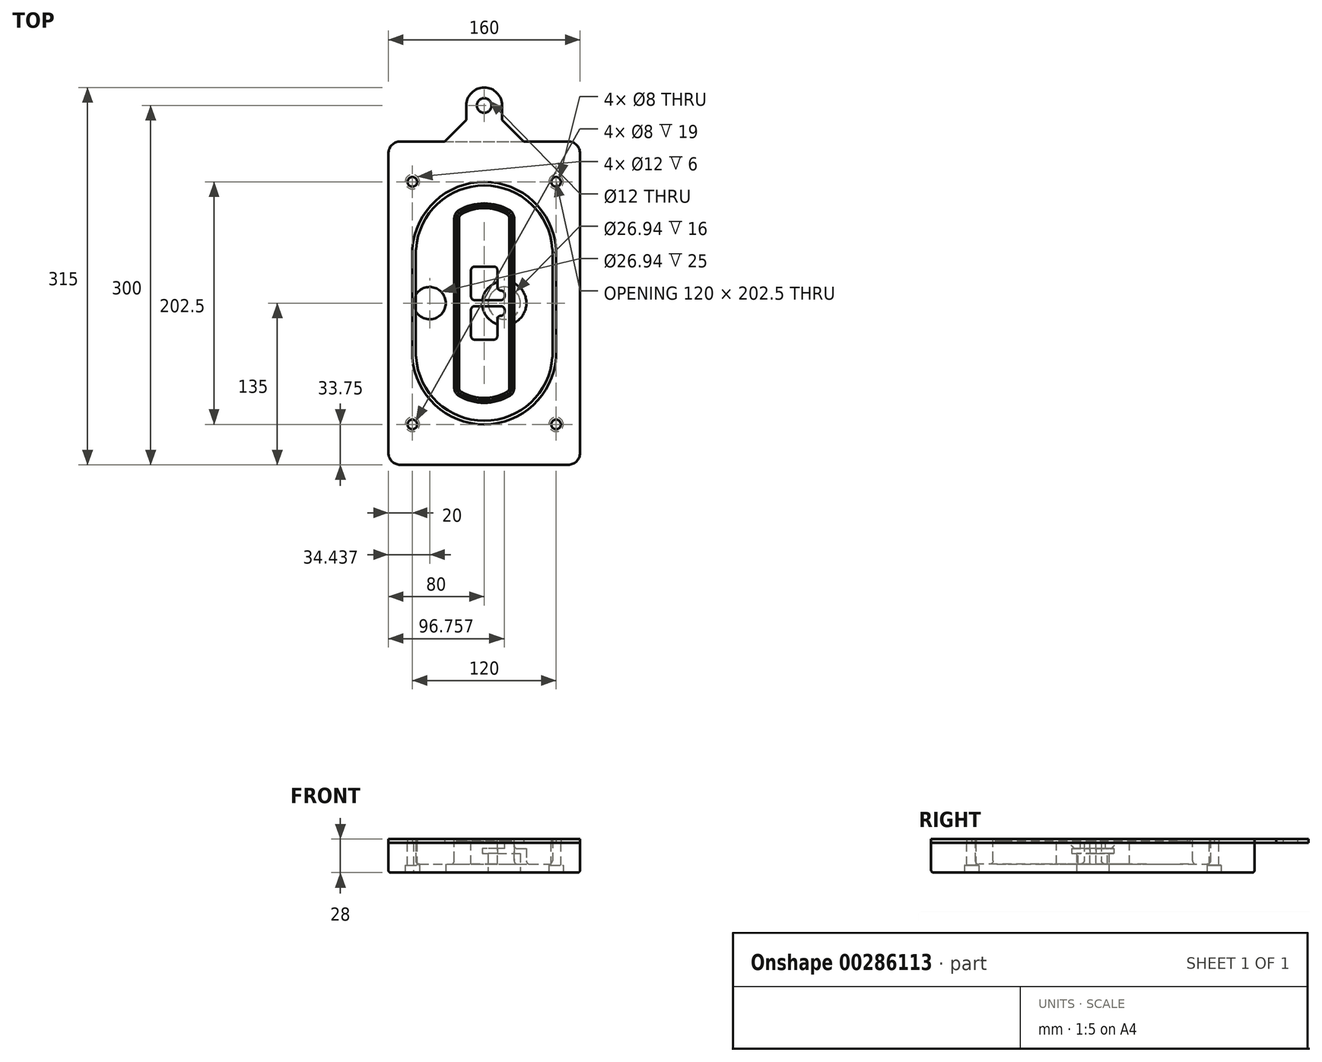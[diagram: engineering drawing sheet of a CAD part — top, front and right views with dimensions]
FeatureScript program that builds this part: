
annotation { "Feature Type Name" : "Feature", "Feature Type Description" : "" }
export const myFeature = defineFeature(function(context is Context, id is Id, definition is map)
    precondition{}
    {
        {
            var Q0;
            Q0=qCreatedBy(makeId("Top.planeOp"),FACE);
            var sketch = newSketch(context, id + "F0", { "sketchPlane" : qUnion([Q0])});
            skPoint(sketch, "E0.rect.middle", {"position": v(0, 0) * mm});
            skLineSegment(sketch, "E1.bottom", {"start": v(-70, -135) * mm, "end": v(70, -135) * mm});
            skLineSegment(sketch, "E1.top", {"start": v(-70, 135) * mm, "end": v(70, 135) * mm});
            skLineSegment(sketch, "E1.left", {"start": v(-80, -125) * mm, "end": v(-80, 125) * mm});
            skLineSegment(sketch, "E1.right", {"start": v(80, -125) * mm, "end": v(80, 125) * mm});
            skLineSegment(sketch, "E2", {"start": v(-80, 135) * mm, "end": v(80, -135) * mm, "construction": true});
            skLineSegment(sketch, "E3", {"start": v(80, 135) * mm, "end": v(-80, -135) * mm, "construction": true});
            skCircle(sketch, "E4", {"center": v(-60, 101.25) * mm, "radius": 4 * mm});
            skCircle(sketch, "E5", {"center": v(60, 101.25) * mm, "radius": 4 * mm});
            skCircle(sketch, "E6", {"center": v(60, -101.25) * mm, "radius": 4 * mm});
            skCircle(sketch, "E7", {"center": v(-60, -101.25) * mm, "radius": 4 * mm});
            skLineSegment(sketch, "E8", {"start": v(-60, 101.25) * mm, "end": v(60, 101.25) * mm, "construction": true});
            skLineSegment(sketch, "E9", {"start": v(60, 101.25) * mm, "end": v(60, -101.25) * mm, "construction": true});
            skLineSegment(sketch, "E10", {"start": v(60, -101.25) * mm, "end": v(-60, -101.25) * mm, "construction": true});
            skLineSegment(sketch, "E11", {"start": v(-60, -101.25) * mm, "end": v(-60, 101.25) * mm, "construction": true});
            skLineSegment(sketch, "E12", {"start": v(-60, 44.66) * mm, "end": v(-60, -44.66) * mm});
            skLineSegment(sketch, "E13", {"start": v(60, 44.66) * mm, "end": v(60, -44.66) * mm});
            skArc(sketch, "E14", {"start": v(59.98, 45.37) * mm, "mid": v(0, 101.25) * mm, "end": v(-59.98, 45.37) * mm});
            skArc(sketch, "E15", {"start": v(-59.98, -45.37) * mm, "mid": v(0, -101.25) * mm, "end": v(59.98, -45.37) * mm});
            skLineSegment(sketch, "E16", {"start": v(-60, 0) * mm, "end": v(60, 0) * mm, "construction": true});
            skPoint(sketch, "E17.visualSharp", {"position": v(-60, -45) * mm});
            skArc(sketch, "E17.filletArc", {"start": v(-60, -44.66) * mm, "mid": v(-60, -45.02) * mm, "end": v(-59.98, -45.37) * mm});
            skPoint(sketch, "E18.visualSharp", {"position": v(-60, 45) * mm});
            skArc(sketch, "E18.filletArc", {"start": v(-59.98, 45.37) * mm, "mid": v(-60, 45.02) * mm, "end": v(-60, 44.66) * mm});
            skPoint(sketch, "E19.visualSharp", {"position": v(60, 45) * mm});
            skArc(sketch, "E19.filletArc", {"start": v(60, 44.66) * mm, "mid": v(60, 45.02) * mm, "end": v(59.98, 45.37) * mm});
            skPoint(sketch, "E20.visualSharp", {"position": v(60, -45) * mm});
            skArc(sketch, "E20.filletArc", {"start": v(59.98, -45.37) * mm, "mid": v(60, -45.02) * mm, "end": v(60, -44.66) * mm});
            skPoint(sketch, "E21.visualSharp", {"position": v(-80, 135) * mm});
            skArc(sketch, "E21.filletArc", {"start": v(-70, 135) * mm, "mid": v(-77.07, 132.07) * mm, "end": v(-80, 125) * mm});
            skPoint(sketch, "E22.visualSharp", {"position": v(80, 135) * mm});
            skArc(sketch, "E22.filletArc", {"start": v(80, 125) * mm, "mid": v(77.07, 132.07) * mm, "end": v(70, 135) * mm});
            skPoint(sketch, "E23.visualSharp", {"position": v(80, -135) * mm});
            skArc(sketch, "E23.filletArc", {"start": v(70, -135) * mm, "mid": v(77.07, -132.07) * mm, "end": v(80, -125) * mm});
            skPoint(sketch, "E24.visualSharp", {"position": v(-80, -135) * mm});
            skArc(sketch, "E24.filletArc", {"start": v(-80, -125) * mm, "mid": v(-77.07, -132.07) * mm, "end": v(-70, -135) * mm});
            skArc(sketch, "E25.0", {"start": v(57, 44.66) * mm, "mid": v(57, 44.9) * mm, "end": v(56.98, 45.16) * mm});
            skLineSegment(sketch, "E25.1", {"start": v(57, 44.66) * mm, "end": v(57, -44.66) * mm});
            skArc(sketch, "E25.2", {"start": v(56.98, -45.16) * mm, "mid": v(57, -44.9) * mm, "end": v(57, -44.66) * mm});
            skArc(sketch, "E25.3", {"start": v(-56.98, -45.16) * mm, "mid": v(0, -98.25) * mm, "end": v(56.98, -45.16) * mm});
            skArc(sketch, "E25.4", {"start": v(-57, -44.66) * mm, "mid": v(-57, -44.9) * mm, "end": v(-56.98, -45.16) * mm});
            skArc(sketch, "E25.5", {"start": v(56.98, 45.16) * mm, "mid": v(0, 98.25) * mm, "end": v(-56.98, 45.16) * mm});
            skLineSegment(sketch, "E25.6", {"start": v(-57, 44.66) * mm, "end": v(-57, -44.66) * mm});
            skArc(sketch, "E25.7", {"start": v(-56.98, 45.16) * mm, "mid": v(-57, 44.9) * mm, "end": v(-57, 44.66) * mm});
            skArc(sketch, "E26.0", {"start": v(-63.97, 45.65) * mm, "mid": v(-64, 45.16) * mm, "end": v(-64, 44.66) * mm});
            skArc(sketch, "E26.1", {"start": v(63.97, 45.65) * mm, "mid": v(0, 105.25) * mm, "end": v(-63.97, 45.65) * mm});
            skArc(sketch, "E26.2", {"start": v(64, 44.66) * mm, "mid": v(64, 45.16) * mm, "end": v(63.97, 45.65) * mm});
            skLineSegment(sketch, "E26.3", {"start": v(64, 44.66) * mm, "end": v(64, -44.66) * mm});
            skArc(sketch, "E26.4", {"start": v(63.97, -45.65) * mm, "mid": v(64, -45.16) * mm, "end": v(64, -44.66) * mm});
            skLineSegment(sketch, "E26.5", {"start": v(-64, 44.66) * mm, "end": v(-64, -44.66) * mm});
            skArc(sketch, "E26.6", {"start": v(-63.97, -45.65) * mm, "mid": v(0, -105.25) * mm, "end": v(63.97, -45.65) * mm});
            skArc(sketch, "E26.7", {"start": v(-64, -44.66) * mm, "mid": v(-64, -45.16) * mm, "end": v(-63.97, -45.65) * mm});
            skSolve(sketch);
        }
        {
            var Q0;
            Q0=makeQuery(id+"F0.imprint","IMPRINT",FACE,{"disambiguationData":[TD([[makeQuery(id+"F0.imprint","IMPRINT",EDGE,{"derivedFrom":sQuery(id+"F0.wireOp",EDGE,"E1.bottom")}),1.0]])]});
            var Q1;
            Q1=makeQuery(id+"F0.imprint","IMPRINT",FACE,{"disambiguationData":[TD([[makeQuery(id+"F0.imprint","IMPRINT",EDGE,{"derivedFrom":sQuery(id+"F0.wireOp",EDGE,"E12")}),1.0]])]});
            var Q2;
            Q2=makeQuery(id+"F0.imprint","IMPRINT",FACE,{"disambiguationData":[TD([[makeQuery(id+"F0.imprint","IMPRINT",EDGE,{"derivedFrom":sQuery(id+"F0.wireOp",EDGE,"E25.0")}),1.0]])]});
            var Q3;
            Q3=makeQuery(id+"F0.imprint","IMPRINT",FACE,{"disambiguationData":[TD([[makeQuery(id+"F0.imprint","IMPRINT",EDGE,{"derivedFrom":sQuery(id+"F0.wireOp",EDGE,"E12")}),-1.0]])]});
            extrude(context, id + "F1", {"entities" : qUnion([Q0, Q1, Q2, Q3]), "oppositeDirection" : true, "depth" : 25 * mm});
        }
        {
            var Q0;
            Q0=makeQuery(id+"F0.imprint","IMPRINT",FACE,{"disambiguationData":[TD([[makeQuery(id+"F0.imprint","IMPRINT",EDGE,{"derivedFrom":sQuery(id+"F0.wireOp",EDGE,"E12")}),1.0]])]});
            extrude(context, id + "F2", {"entities" : qUnion([Q0]), "operationType" : NewBodyOperationType.ADD, "depth" : 3 * mm});
        }
        {
            var Q0;
            Q0=makeQuery(id+"F0.imprint","IMPRINT",FACE,{"disambiguationData":[TD([[makeQuery(id+"F0.imprint","IMPRINT",EDGE,{"derivedFrom":sQuery(id+"F0.wireOp",EDGE,"E25.0")}),1.0]])]});
            extrude(context, id + "F3", {"entities" : qUnion([Q0]), "operationType" : NewBodyOperationType.REMOVE, "oppositeDirection" : true, "depth" : 18 * mm});
        }
        {
            var Q0;
            Q0=makeQuery(id+"F2.opExtrude","CAP_FACE",FACE,{"disambiguationData":[OSD([sQuery(id+"F0.wireOp",EDGE,"E12"),sQuery(id+"F0.wireOp",EDGE,"E13"),sQuery(id+"F0.wireOp",EDGE,"E14"),sQuery(id+"F0.wireOp",EDGE,"E15"),sQuery(id+"F0.wireOp",EDGE,"E17.filletArc"),sQuery(id+"F0.wireOp",EDGE,"E18.filletArc"),sQuery(id+"F0.wireOp",EDGE,"E19.filletArc"),sQuery(id+"F0.wireOp",EDGE,"E20.filletArc"),sQuery(id+"F0.wireOp",EDGE,"E25.0"),sQuery(id+"F0.wireOp",EDGE,"E25.1"),sQuery(id+"F0.wireOp",EDGE,"E25.2"),sQuery(id+"F0.wireOp",EDGE,"E25.3"),sQuery(id+"F0.wireOp",EDGE,"E25.4"),sQuery(id+"F0.wireOp",EDGE,"E25.5"),sQuery(id+"F0.wireOp",EDGE,"E25.6"),sQuery(id+"F0.wireOp",EDGE,"E25.7")])],"isStart":false});
            var sketch = newSketch(context, id + "F4", { "sketchPlane" : qUnion([Q0])});
            skArc(sketch, "E27.0", {"start": v(-20.99, -77.65) * mm, "mid": v(0, -83.25) * mm, "end": v(20.99, -77.65) * mm});
            skArc(sketch, "E28.0", {"start": v(20.99, 77.65) * mm, "mid": v(0, 83.25) * mm, "end": v(-20.99, 77.65) * mm});
            skLineSegment(sketch, "E29", {"start": v(-25, 70.71) * mm, "end": v(-25, -70.71) * mm});
            skLineSegment(sketch, "E30", {"start": v(25, 70.71) * mm, "end": v(25, -70.71) * mm});
            skLineSegment(sketch, "E31", {"start": v(-25, 75.03) * mm, "end": v(25, 75.03) * mm, "construction": true});
            skLineSegment(sketch, "E32", {"start": v(-25, -75.03) * mm, "end": v(25, -75.03) * mm, "construction": true});
            skPoint(sketch, "E33.visualSharp", {"position": v(-25, 75.03) * mm});
            skArc(sketch, "E33.filletArc", {"start": v(-20.99, 77.65) * mm, "mid": v(-23.92, 74.72) * mm, "end": v(-25, 70.71) * mm});
            skPoint(sketch, "E34.visualSharp", {"position": v(25, 75.03) * mm});
            skArc(sketch, "E34.filletArc", {"start": v(25, 70.71) * mm, "mid": v(23.92, 74.72) * mm, "end": v(20.99, 77.65) * mm});
            skPoint(sketch, "E35.visualSharp", {"position": v(25, -75.03) * mm});
            skArc(sketch, "E35.filletArc", {"start": v(20.99, -77.65) * mm, "mid": v(23.92, -74.72) * mm, "end": v(25, -70.71) * mm});
            skPoint(sketch, "E36.visualSharp", {"position": v(-25, -75.03) * mm});
            skArc(sketch, "E36.filletArc", {"start": v(-25, -70.71) * mm, "mid": v(-23.92, -74.72) * mm, "end": v(-20.99, -77.65) * mm});
            skArc(sketch, "E37.0", {"start": v(56.98, 45.16) * mm, "mid": v(0, 98.25) * mm, "end": v(-56.98, 45.16) * mm});
            skArc(sketch, "E37.1", {"start": v(-56.98, 45.16) * mm, "mid": v(-57, 44.9) * mm, "end": v(-57, 44.66) * mm});
            skLineSegment(sketch, "E37.2", {"start": v(-57, 44.66) * mm, "end": v(-57, -44.66) * mm});
            skArc(sketch, "E37.3", {"start": v(-57, -44.66) * mm, "mid": v(-57, -44.9) * mm, "end": v(-56.98, -45.16) * mm});
            skArc(sketch, "E37.4", {"start": v(-56.98, -45.16) * mm, "mid": v(0, -98.25) * mm, "end": v(56.98, -45.16) * mm});
            skArc(sketch, "E37.5", {"start": v(56.98, -45.16) * mm, "mid": v(57, -44.9) * mm, "end": v(57, -44.66) * mm});
            skLineSegment(sketch, "E37.6", {"start": v(57, 44.66) * mm, "end": v(57, -44.66) * mm});
            skArc(sketch, "E37.7", {"start": v(57, 44.66) * mm, "mid": v(57, 44.9) * mm, "end": v(56.98, 45.16) * mm});
            skLineSegment(sketch, "E38.0", {"start": v(23, 70.71) * mm, "end": v(23, -70.71) * mm});
            skArc(sketch, "E38.1", {"start": v(19.99, -75.92) * mm, "mid": v(22.2, -73.72) * mm, "end": v(23, -70.71) * mm});
            skArc(sketch, "E38.2", {"start": v(-19.99, -75.92) * mm, "mid": v(0, -81.25) * mm, "end": v(19.99, -75.92) * mm});
            skArc(sketch, "E38.3", {"start": v(-23, -70.71) * mm, "mid": v(-22.2, -73.72) * mm, "end": v(-19.99, -75.92) * mm});
            skLineSegment(sketch, "E38.4", {"start": v(-23, 70.71) * mm, "end": v(-23, -70.71) * mm});
            skArc(sketch, "E38.5", {"start": v(23, 70.71) * mm, "mid": v(22.2, 73.72) * mm, "end": v(19.99, 75.92) * mm});
            skArc(sketch, "E38.6", {"start": v(-19.99, 75.92) * mm, "mid": v(-22.2, 73.72) * mm, "end": v(-23, 70.71) * mm});
            skArc(sketch, "E38.7", {"start": v(19.99, 75.92) * mm, "mid": v(0, 81.25) * mm, "end": v(-19.99, 75.92) * mm});
            skArc(sketch, "E39.0", {"start": v(21, 70.71) * mm, "mid": v(20.46, 72.72) * mm, "end": v(19, 74.18) * mm});
            skLineSegment(sketch, "E39.1", {"start": v(21, 70.71) * mm, "end": v(21, -70.71) * mm});
            skArc(sketch, "E39.2", {"start": v(19, -74.18) * mm, "mid": v(20.46, -72.72) * mm, "end": v(21, -70.71) * mm});
            skArc(sketch, "E39.3", {"start": v(-19, -74.18) * mm, "mid": v(0, -79.25) * mm, "end": v(19, -74.18) * mm});
            skArc(sketch, "E39.4", {"start": v(-21, -70.71) * mm, "mid": v(-20.46, -72.72) * mm, "end": v(-19, -74.18) * mm});
            skArc(sketch, "E39.5", {"start": v(19, 74.18) * mm, "mid": v(0, 79.25) * mm, "end": v(-19, 74.18) * mm});
            skLineSegment(sketch, "E39.6", {"start": v(-21, 70.71) * mm, "end": v(-21, -70.71) * mm});
            skArc(sketch, "E39.7", {"start": v(-19, 74.18) * mm, "mid": v(-20.46, 72.72) * mm, "end": v(-21, 70.71) * mm});
            skLineSegment(sketch, "E40", {"start": v(-25, 0) * mm, "end": v(25, 0) * mm, "construction": true});
            skLineSegment(sketch, "E41", {"start": v(-11, 5.5) * mm, "end": v(-11, 27.5) * mm});
            skLineSegment(sketch, "E42", {"start": v(-8, 30.5) * mm, "end": v(8, 30.5) * mm});
            skLineSegment(sketch, "E43", {"start": v(11, 27.5) * mm, "end": v(11, 13.5) * mm});
            skLineSegment(sketch, "E44", {"start": v(14, 10.5) * mm, "end": v(14, 10.5) * mm});
            skLineSegment(sketch, "E45", {"start": v(17, 7.5) * mm, "end": v(17, 5.5) * mm});
            skLineSegment(sketch, "E46", {"start": v(14, 2.5) * mm, "end": v(-8, 2.5) * mm});
            skPoint(sketch, "E47.visualSharp", {"position": v(-11, 30.5) * mm});
            skArc(sketch, "E47.filletArc", {"start": v(-8, 30.5) * mm, "mid": v(-10.12, 29.62) * mm, "end": v(-11, 27.5) * mm});
            skPoint(sketch, "E48.visualSharp", {"position": v(11, 30.5) * mm});
            skArc(sketch, "E48.filletArc", {"start": v(11, 27.5) * mm, "mid": v(10.12, 29.62) * mm, "end": v(8, 30.5) * mm});
            skPoint(sketch, "E49.visualSharp", {"position": v(11, 10.5) * mm});
            skArc(sketch, "E49.filletArc", {"start": v(11, 13.5) * mm, "mid": v(11.88, 11.38) * mm, "end": v(14, 10.5) * mm});
            skPoint(sketch, "E50.visualSharp", {"position": v(17, 10.5) * mm});
            skArc(sketch, "E50.filletArc", {"start": v(17, 7.5) * mm, "mid": v(16.12, 9.62) * mm, "end": v(14, 10.5) * mm});
            skPoint(sketch, "E51.visualSharp", {"position": v(17, 2.5) * mm});
            skArc(sketch, "E51.filletArc", {"start": v(14, 2.5) * mm, "mid": v(16.12, 3.38) * mm, "end": v(17, 5.5) * mm});
            skPoint(sketch, "E52.visualSharp", {"position": v(-11, 2.5) * mm});
            skArc(sketch, "E52.filletArc", {"start": v(-11, 5.5) * mm, "mid": v(-10.12, 3.38) * mm, "end": v(-8, 2.5) * mm});
            skLineSegment(sketch, "E53.0.MirrorCS", {"start": v(14, -2.5) * mm, "end": v(-8, -2.5) * mm});
            skArc(sketch, "E54.0.MirrorCS", {"start": v(-11, -5.5) * mm, "mid": v(-10.12, -3.38) * mm, "end": v(-8, -2.5) * mm});
            skLineSegment(sketch, "E55.0.MirrorCS", {"start": v(-11, -5.5) * mm, "end": v(-11, -27.5) * mm});
            skArc(sketch, "E56.0.MirrorCS", {"start": v(-8, -30.5) * mm, "mid": v(-10.12, -29.62) * mm, "end": v(-11, -27.5) * mm});
            skLineSegment(sketch, "E57.0.MirrorCS", {"start": v(-8, -30.5) * mm, "end": v(8, -30.5) * mm});
            skArc(sketch, "E58.0.MirrorCS", {"start": v(11, -27.5) * mm, "mid": v(10.12, -29.62) * mm, "end": v(8, -30.5) * mm});
            skLineSegment(sketch, "E59.0.MirrorCS", {"start": v(11, -27.5) * mm, "end": v(11, -13.5) * mm});
            skArc(sketch, "E60.0.MirrorCS", {"start": v(11, -13.5) * mm, "mid": v(11.88, -11.38) * mm, "end": v(14, -10.5) * mm});
            skArc(sketch, "E61.0.MirrorCS", {"start": v(17, -7.5) * mm, "mid": v(16.12, -9.62) * mm, "end": v(14, -10.5) * mm});
            skLineSegment(sketch, "E62.0.MirrorCS", {"start": v(17, -7.5) * mm, "end": v(17, -5.5) * mm});
            skArc(sketch, "E63.0.MirrorCS", {"start": v(14, -2.5) * mm, "mid": v(16.12, -3.38) * mm, "end": v(17, -5.5) * mm});
            skSolve(sketch);
        }
        {
            var Q0;
            Q0=makeQuery(id+"F4.imprint","IMPRINT",FACE,{"disambiguationData":[TD([[makeQuery(id+"F4.imprint","IMPRINT",EDGE,{"derivedFrom":sQuery(id+"F4.wireOp",EDGE,"E27.0")}),1.0]])]});
            var Q1;
            Q1=makeQuery(id+"F4.imprint","IMPRINT",FACE,{"disambiguationData":[TD([[makeQuery(id+"F4.imprint","IMPRINT",EDGE,{"derivedFrom":sQuery(id+"F4.wireOp",EDGE,"E38.0")}),-1.0]])]});
            var Q2;
            Q2=makeQuery(id+"F4.imprint","IMPRINT",FACE,{"disambiguationData":[TD([[makeQuery(id+"F4.imprint","IMPRINT",EDGE,{"derivedFrom":sQuery(id+"F4.wireOp",EDGE,"E39.0")}),1.0]])]});
            extrude(context, id + "F5", {"entities" : qUnion([Q0, Q1, Q2]), "operationType" : NewBodyOperationType.ADD, "endBound" : BoundingType.UP_TO_NEXT, "oppositeDirection" : true, "depth" : 25 * mm});
        }
        {
            var Q0;
            Q0=makeQuery(id+"F4.imprint","IMPRINT",FACE,{"disambiguationData":[TD([[makeQuery(id+"F4.imprint","IMPRINT",EDGE,{"derivedFrom":sQuery(id+"F4.wireOp",EDGE,"E38.0")}),-1.0]])]});
            extrude(context, id + "F6", {"entities" : qUnion([Q0]), "operationType" : NewBodyOperationType.REMOVE, "oppositeDirection" : true, "depth" : 2 * mm});
        }
        {
            var Q0;
            Q0=makeQuery(id+"F1.opExtrude","CAP_FACE",FACE,{"disambiguationData":[OSD([sQuery(id+"F0.wireOp",EDGE,"E1.bottom"),sQuery(id+"F0.wireOp",EDGE,"E1.top"),sQuery(id+"F0.wireOp",EDGE,"E1.left"),sQuery(id+"F0.wireOp",EDGE,"E1.right"),sQuery(id+"F0.wireOp",EDGE,"E4"),sQuery(id+"F0.wireOp",EDGE,"E5"),sQuery(id+"F0.wireOp",EDGE,"E6"),sQuery(id+"F0.wireOp",EDGE,"E7"),sQuery(id+"F0.wireOp",EDGE,"E21.filletArc"),sQuery(id+"F0.wireOp",EDGE,"E22.filletArc"),sQuery(id+"F0.wireOp",EDGE,"E23.filletArc"),sQuery(id+"F0.wireOp",EDGE,"E24.filletArc")])],"isStart":false});
            var sketch = newSketch(context, id + "F7", { "sketchPlane" : qUnion([Q0])});
            skCircle(sketch, "E64", {"center": v(16.76, 0) * mm, "radius": 13.47 * mm});
            skCircle(sketch, "E65", {"center": v(-45.56, 0) * mm, "radius": 13.47 * mm});
            skLineSegment(sketch, "E66", {"start": v(80, 0) * mm, "end": v(-80, 0) * mm});
            skCircle(sketch, "E67", {"center": v(16.76, 0) * mm, "radius": 18.47 * mm});
            skCircle(sketch, "E68", {"center": v(60, -101.25) * mm, "radius": 6 * mm});
            skCircle(sketch, "E69", {"center": v(-60, -101.25) * mm, "radius": 6 * mm});
            skCircle(sketch, "E70", {"center": v(-60, 101.25) * mm, "radius": 6 * mm});
            skCircle(sketch, "E71", {"center": v(60, 101.25) * mm, "radius": 6 * mm});
            skSolve(sketch);
        }
        {
            var Q0;
            {var subQ1=sQuery(id+"F7.wireOp",EDGE,"E66");var subQ4=sQuery(id+"F7.wireOp",EDGE,"E64");var subQ6=makeQuery(id+"F7.imprint","INTERSECT",VERTEX,{"disambiguationData":[OD(0.0)],"derivedFrom":[subQ4,subQ1]});Q0=makeQuery(id+"F7.imprint","IMPRINT",FACE,{"disambiguationData":[TD([[makeQuery(id+"F7.imprint","IMPRINT",EDGE,{"disambiguationData":[TD([[subQ6,-1.0]])],"derivedFrom":subQ4}),-1.0]])]});}
            var Q1;
            {var subQ0=sQuery(id+"F7.wireOp",EDGE,"E66");var subQ1=sQuery(id+"F7.wireOp",EDGE,"E64");var subQ3=makeQuery(id+"F7.imprint","INTERSECT",VERTEX,{"disambiguationData":[OD(0.0)],"derivedFrom":[subQ1,subQ0]});Q1=makeQuery(id+"F7.imprint","IMPRINT",FACE,{"disambiguationData":[TD([[makeQuery(id+"F7.imprint","IMPRINT",EDGE,{"disambiguationData":[TD([[subQ3,-1.0]])],"derivedFrom":subQ1}),1.0]])]});}
            var Q2;
            {var subQ0=sQuery(id+"F7.wireOp",EDGE,"E66");var subQ1=sQuery(id+"F7.wireOp",EDGE,"E64");var subQ3=makeQuery(id+"F7.imprint","INTERSECT",VERTEX,{"disambiguationData":[OD(0.0)],"derivedFrom":[subQ1,subQ0]});Q2=makeQuery(id+"F7.imprint","IMPRINT",FACE,{"disambiguationData":[TD([[makeQuery(id+"F7.imprint","IMPRINT",EDGE,{"disambiguationData":[TD([[subQ3,1.0]])],"derivedFrom":subQ1}),1.0]])]});}
            var Q3;
            {var subQ1=sQuery(id+"F7.wireOp",EDGE,"E66");var subQ4=sQuery(id+"F7.wireOp",EDGE,"E64");var subQ6=makeQuery(id+"F7.imprint","INTERSECT",VERTEX,{"disambiguationData":[OD(0.0)],"derivedFrom":[subQ4,subQ1]});Q3=makeQuery(id+"F7.imprint","IMPRINT",FACE,{"disambiguationData":[TD([[makeQuery(id+"F7.imprint","IMPRINT",EDGE,{"disambiguationData":[TD([[subQ6,1.0]])],"derivedFrom":subQ4}),-1.0]])]});}
            extrude(context, id + "F8", {"entities" : qUnion([Q0, Q1, Q2, Q3]), "operationType" : NewBodyOperationType.ADD, "oppositeDirection" : true, "depth" : 20 * mm});
        }
        {
            var Q0;
            {var subQ0=sQuery(id+"F7.wireOp",EDGE,"E66");var subQ1=sQuery(id+"F7.wireOp",EDGE,"E64");var subQ3=makeQuery(id+"F7.imprint","INTERSECT",VERTEX,{"disambiguationData":[OD(0.0)],"derivedFrom":[subQ1,subQ0]});Q0=makeQuery(id+"F7.imprint","IMPRINT",FACE,{"disambiguationData":[TD([[makeQuery(id+"F7.imprint","IMPRINT",EDGE,{"disambiguationData":[TD([[subQ3,-1.0]])],"derivedFrom":subQ1}),1.0]])]});}
            var Q1;
            {var subQ0=sQuery(id+"F7.wireOp",EDGE,"E66");var subQ1=sQuery(id+"F7.wireOp",EDGE,"E64");var subQ3=makeQuery(id+"F7.imprint","INTERSECT",VERTEX,{"disambiguationData":[OD(0.0)],"derivedFrom":[subQ1,subQ0]});Q1=makeQuery(id+"F7.imprint","IMPRINT",FACE,{"disambiguationData":[TD([[makeQuery(id+"F7.imprint","IMPRINT",EDGE,{"disambiguationData":[TD([[subQ3,1.0]])],"derivedFrom":subQ1}),1.0]])]});}
            extrude(context, id + "F9", {"entities" : qUnion([Q0, Q1]), "operationType" : NewBodyOperationType.REMOVE, "oppositeDirection" : true, "depth" : 16 * mm});
        }
        {
            var Q0;
            {var subQ0=sQuery(id+"F7.wireOp",EDGE,"E66");var subQ1=sQuery(id+"F7.wireOp",EDGE,"E65");var subQ3=makeQuery(id+"F7.imprint","INTERSECT",VERTEX,{"disambiguationData":[OD(0.0)],"derivedFrom":[subQ1,subQ0]});Q0=makeQuery(id+"F7.imprint","IMPRINT",FACE,{"disambiguationData":[TD([[makeQuery(id+"F7.imprint","IMPRINT",EDGE,{"disambiguationData":[TD([[subQ3,-1.0]])],"derivedFrom":subQ1}),1.0]])]});}
            var Q1;
            {var subQ0=sQuery(id+"F7.wireOp",EDGE,"E66");var subQ1=sQuery(id+"F7.wireOp",EDGE,"E65");var subQ3=makeQuery(id+"F7.imprint","INTERSECT",VERTEX,{"disambiguationData":[OD(0.0)],"derivedFrom":[subQ1,subQ0]});Q1=makeQuery(id+"F7.imprint","IMPRINT",FACE,{"disambiguationData":[TD([[makeQuery(id+"F7.imprint","IMPRINT",EDGE,{"disambiguationData":[TD([[subQ3,1.0]])],"derivedFrom":subQ1}),1.0]])]});}
            extrude(context, id + "F10", {"entities" : qUnion([Q0, Q1]), "operationType" : NewBodyOperationType.REMOVE, "oppositeDirection" : true, "depth" : 25 * mm});
        }
        {
            var Q0;
            Q0=makeQuery(id+"F7.imprint","IMPRINT",FACE,{"disambiguationData":[TD([[makeQuery(id+"F7.imprint","IMPRINT",EDGE,{"derivedFrom":sQuery(id+"F7.wireOp",EDGE,"E68")}),1.0]])]});
            var Q1;
            Q1=makeQuery(id+"F7.imprint","IMPRINT",FACE,{"disambiguationData":[TD([[makeQuery(id+"F7.imprint","IMPRINT",EDGE,{"derivedFrom":makeQuery(id+"F1.opExtrude","CAP_EDGE",EDGE,{"disambiguationData":[OSD([sQuery(id+"F0.wireOp",EDGE,"E5")])],"isStart":false})}),-1.0]])]});
            var Q2;
            Q2=makeQuery(id+"F7.imprint","IMPRINT",FACE,{"disambiguationData":[TD([[makeQuery(id+"F7.imprint","IMPRINT",EDGE,{"derivedFrom":sQuery(id+"F7.wireOp",EDGE,"E69")}),1.0]])]});
            var Q3;
            Q3=makeQuery(id+"F7.imprint","IMPRINT",FACE,{"disambiguationData":[TD([[makeQuery(id+"F7.imprint","IMPRINT",EDGE,{"derivedFrom":makeQuery(id+"F1.opExtrude","CAP_EDGE",EDGE,{"disambiguationData":[OSD([sQuery(id+"F0.wireOp",EDGE,"E4")])],"isStart":false})}),-1.0]])]});
            var Q4;
            Q4=makeQuery(id+"F7.imprint","IMPRINT",FACE,{"disambiguationData":[TD([[makeQuery(id+"F7.imprint","IMPRINT",EDGE,{"derivedFrom":sQuery(id+"F7.wireOp",EDGE,"E70")}),1.0]])]});
            var Q5;
            Q5=makeQuery(id+"F7.imprint","IMPRINT",FACE,{"disambiguationData":[TD([[makeQuery(id+"F7.imprint","IMPRINT",EDGE,{"derivedFrom":makeQuery(id+"F1.opExtrude","CAP_EDGE",EDGE,{"disambiguationData":[OSD([sQuery(id+"F0.wireOp",EDGE,"E7")])],"isStart":false})}),-1.0]])]});
            var Q6;
            Q6=makeQuery(id+"F7.imprint","IMPRINT",FACE,{"disambiguationData":[TD([[makeQuery(id+"F7.imprint","IMPRINT",EDGE,{"derivedFrom":sQuery(id+"F7.wireOp",EDGE,"E71")}),1.0]])]});
            var Q7;
            Q7=makeQuery(id+"F7.imprint","IMPRINT",FACE,{"disambiguationData":[TD([[makeQuery(id+"F7.imprint","IMPRINT",EDGE,{"derivedFrom":makeQuery(id+"F1.opExtrude","CAP_EDGE",EDGE,{"disambiguationData":[OSD([sQuery(id+"F0.wireOp",EDGE,"E6")])],"isStart":false})}),-1.0]])]});
            extrude(context, id + "F11", {"entities" : qUnion([Q0, Q1, Q2, Q3, Q4, Q5, Q6, Q7]), "operationType" : NewBodyOperationType.REMOVE, "oppositeDirection" : true, "depth" : 6 * mm});
        }
        {
            var Q0;
            Q0=makeQuery(id+"F9.boolean.opBoolean","COPY",FACE,{"derivedFrom":makeQuery(id+"F9.opExtrude","CAP_FACE",FACE,{"disambiguationData":[OSD([sQuery(id+"F7.wireOp",EDGE,"E64")])],"isStart":false})});
            var sketch = newSketch(context, id + "F12", { "sketchPlane" : qUnion([Q0])});
            skArc(sketch, "E72.0", {"start": v(11, 17.55) * mm, "mid": v(2.57, 11.82) * mm, "end": v(-1.54, 2.5) * mm});
            skArc(sketch, "E72.1", {"start": v(-1.54, -2.5) * mm, "mid": v(2.57, -11.82) * mm, "end": v(11, -17.55) * mm});
            skLineSegment(sketch, "E73", {"start": v(-1.54, -2.5) * mm, "end": v(14, -2.5) * mm});
            skLineSegment(sketch, "E74.0", {"start": v(14, 2.5) * mm, "end": v(-1.54, 2.5) * mm});
            skArc(sketch, "E74.1", {"start": v(14, 2.5) * mm, "mid": v(16.12, 3.38) * mm, "end": v(17, 5.5) * mm});
            skLineSegment(sketch, "E74.2", {"start": v(17, 7.5) * mm, "end": v(17, 5.5) * mm});
            skArc(sketch, "E74.3", {"start": v(17, 7.5) * mm, "mid": v(16.12, 9.62) * mm, "end": v(14, 10.5) * mm});
            skArc(sketch, "E74.4", {"start": v(11, 13.5) * mm, "mid": v(11.88, 11.38) * mm, "end": v(14, 10.5) * mm});
            skLineSegment(sketch, "E74.5", {"start": v(11, 17.55) * mm, "end": v(11, 13.5) * mm});
            skLineSegment(sketch, "E74.7", {"start": v(14, -2.5) * mm, "end": v(-1.54, -2.5) * mm});
            skArc(sketch, "E74.8", {"start": v(14, -2.5) * mm, "mid": v(16.12, -3.38) * mm, "end": v(17, -5.5) * mm});
            skLineSegment(sketch, "E74.9", {"start": v(17, -7.5) * mm, "end": v(17, -5.5) * mm});
            skArc(sketch, "E74.10", {"start": v(17, -7.5) * mm, "mid": v(16.12, -9.62) * mm, "end": v(14, -10.5) * mm});
            skArc(sketch, "E74.11", {"start": v(11, -13.5) * mm, "mid": v(11.88, -11.38) * mm, "end": v(14, -10.5) * mm});
            skLineSegment(sketch, "E74.12", {"start": v(11, -17.55) * mm, "end": v(11, -13.5) * mm});
            skPoint(sketch, "E75.orphan", {"position": v(11, -27.5) * mm});
            skPoint(sketch, "E76.orphan", {"position": v(-8, -2.5) * mm});
            skPoint(sketch, "E77.orphan", {"position": v(-8, 2.5) * mm});
            skPoint(sketch, "E78.orphan", {"position": v(11, 27.5) * mm});
            skSolve(sketch);
        }
        {
            var Q0;
            {var subQ7=sQuery(id+"F12.wireOp",EDGE,"E72.0");var subQ14=sQuery(id+"F12.wireOp",EDGE,"E72.1");var subQ16=sQuery(id+"F12.wireOp",EDGE,"E74.1");var subQ18=sQuery(id+"F12.wireOp",EDGE,"E74.8");Q0=qUnion([makeQuery(id+"F12.imprint","IMPRINT",FACE,{"disambiguationData":[TD([[makeQuery(id+"F12.imprint","IMPRINT",EDGE,{"derivedFrom":subQ7}),1.0]])]}),makeQuery(id+"F12.imprint","IMPRINT",FACE,{"disambiguationData":[TD([[makeQuery(id+"F12.imprint","IMPRINT",EDGE,{"derivedFrom":subQ14}),1.0]])]}),makeQuery(id+"F12.imprint","IMPRINT",FACE,{"disambiguationData":[TD([[makeQuery(id+"F12.imprint","IMPRINT",EDGE,{"derivedFrom":subQ16}),1.0]])]}),makeQuery(id+"F12.imprint","IMPRINT",FACE,{"disambiguationData":[TD([[makeQuery(id+"F12.imprint","IMPRINT",EDGE,{"derivedFrom":subQ18}),-1.0]])]})]);}
            var Q1;
            Q1=makeQuery(id+"F5.boolean.opBoolean","SPLIT",FACE,{"disambiguationData":[TD([makeQuery(id+"F5.opExtrude","SWEPT_FACE",FACE,{"disambiguationData":[OSD([sQuery(id+"F4.wireOp",EDGE,"E41")])]})])],"derivedFrom":makeQuery(id+"F3.boolean.opBoolean","COPY",FACE,{"derivedFrom":makeQuery(id+"F3.opExtrude","CAP_FACE",FACE,{"disambiguationData":[OSD([sQuery(id+"F0.wireOp",EDGE,"E25.0"),sQuery(id+"F0.wireOp",EDGE,"E25.1"),sQuery(id+"F0.wireOp",EDGE,"E25.2"),sQuery(id+"F0.wireOp",EDGE,"E25.3"),sQuery(id+"F0.wireOp",EDGE,"E25.4"),sQuery(id+"F0.wireOp",EDGE,"E25.5"),sQuery(id+"F0.wireOp",EDGE,"E25.6"),sQuery(id+"F0.wireOp",EDGE,"E25.7")])],"isStart":false})})});
            extrude(context, id + "F13", {"entities" : qUnion([Q0]), "operationType" : NewBodyOperationType.REMOVE, "endBound" : BoundingType.UP_TO_SURFACE, "endBoundEntityFace" : qUnion([Q1]), "depth" : 25 * mm});
        }
        {
            var Q0;
            Q0=makeQuery(id+"F3.boolean.opBoolean","COPY",EDGE,{"derivedFrom":makeQuery(id+"F3.opExtrude","CAP_EDGE",EDGE,{"disambiguationData":[OSD([sQuery(id+"F0.wireOp",EDGE,"E25.6")])],"isStart":false})});
            var Q1;
            Q1=makeQuery(id+"F8.boolean.opBoolean","INTERSECT",EDGE,{"derivedFrom":[makeQuery(id+"F5.opExtrude","SWEPT_FACE",FACE,{"disambiguationData":[OSD([sQuery(id+"F4.wireOp",EDGE,"E30")])]}),makeQuery(id+"F8.opExtrude","CAP_FACE",FACE,{"disambiguationData":[OSD([sQuery(id+"F7.wireOp",EDGE,"E67")])],"isStart":false})]});
            var Q2;
            Q2=makeQuery(id+"F8.boolean.opBoolean","INTERSECT",EDGE,{"disambiguationData":[OD(1.0)],"derivedFrom":[makeQuery(id+"F5.opExtrude","SWEPT_FACE",FACE,{"disambiguationData":[OSD([sQuery(id+"F4.wireOp",EDGE,"E30")])]}),makeQuery(id+"F8.opExtrude","SWEPT_FACE",FACE,{"disambiguationData":[OSD([sQuery(id+"F7.wireOp",EDGE,"E67")])]})]});
            var Q3;
            {var subQ0=sQuery(id+"F4.wireOp",EDGE,"E30");Q3=makeQuery(id+"F8.boolean.opBoolean","SPLIT",EDGE,{"disambiguationData":[TD([makeQuery(id+"F5.opExtrude","SWEPT_FACE",FACE,{"disambiguationData":[OSD([sQuery(id+"F4.wireOp",EDGE,"E35.filletArc")])]})])],"derivedFrom":makeQuery(id+"F5.opExtrude","CAP_EDGE",EDGE,{"disambiguationData":[OSD([subQ0])],"isStart":false})});}
            var Q4;
            {var subQ0=sQuery(id+"F0.wireOp",EDGE,"E25.7");var subQ1=sQuery(id+"F0.wireOp",EDGE,"E25.1");var subQ2=sQuery(id+"F0.wireOp",EDGE,"E25.6");var subQ3=sQuery(id+"F0.wireOp",EDGE,"E25.5");var subQ4=sQuery(id+"F0.wireOp",EDGE,"E25.4");var subQ5=sQuery(id+"F0.wireOp",EDGE,"E25.0");var subQ6=sQuery(id+"F0.wireOp",EDGE,"E25.2");var subQ7=sQuery(id+"F0.wireOp",EDGE,"E25.3");Q4=makeQuery(id+"F8.boolean.opBoolean","INTERSECT",EDGE,{"derivedFrom":[makeQuery(id+"F5.boolean.opBoolean","SPLIT",FACE,{"disambiguationData":[TD([makeQuery(id+"F2.opExtrude","SWEPT_FACE",FACE,{"disambiguationData":[OSD([subQ5])]})])],"derivedFrom":makeQuery(id+"F3.boolean.opBoolean","COPY",FACE,{"derivedFrom":makeQuery(id+"F3.opExtrude","CAP_FACE",FACE,{"disambiguationData":[OSD([subQ5,subQ1,subQ6,subQ7,subQ4,subQ3,subQ2,subQ0])],"isStart":false})})}),makeQuery(id+"F8.opExtrude","SWEPT_FACE",FACE,{"disambiguationData":[OSD([sQuery(id+"F7.wireOp",EDGE,"E67")])]})]});}
            var Q5;
            Q5=makeQuery(id+"F8.boolean.opBoolean","INTERSECT",EDGE,{"disambiguationData":[OD(0.0)],"derivedFrom":[makeQuery(id+"F5.opExtrude","SWEPT_FACE",FACE,{"disambiguationData":[OSD([sQuery(id+"F4.wireOp",EDGE,"E30")])]}),makeQuery(id+"F8.opExtrude","SWEPT_FACE",FACE,{"disambiguationData":[OSD([sQuery(id+"F7.wireOp",EDGE,"E67")])]})]});
            fillet(context, id + "F14", {"entities" : qUnion([Q0, Q1, Q2, Q3, Q4, Q5]), "radius" : 3 * mm, "tangentPropagation" : true, "allowEdgeOverflow" : false});
        }
        {
            var Q0;
            Q0=makeQuery(id+"F1.opExtrude","CAP_EDGE",EDGE,{"disambiguationData":[OSD([sQuery(id+"F0.wireOp",EDGE,"E1.bottom")])],"isStart":false});
            fillet(context, id + "F15", {"entities" : qUnion([Q0]), "radius" : 2 * mm, "tangentPropagation" : true, "allowEdgeOverflow" : false});
        }
        {
            var Q0;
            {var subQ0=sQuery(id+"F0.wireOp",EDGE,"E21.filletArc");var subQ1=sQuery(id+"F0.wireOp",EDGE,"E7");var subQ2=sQuery(id+"F0.wireOp",EDGE,"E6");var subQ3=sQuery(id+"F0.wireOp",EDGE,"E5");var subQ4=sQuery(id+"F0.wireOp",EDGE,"E4");var subQ5=sQuery(id+"F0.wireOp",EDGE,"E22.filletArc");var subQ6=sQuery(id+"F0.wireOp",EDGE,"E1.bottom");var subQ7=sQuery(id+"F0.wireOp",EDGE,"E1.right");var subQ8=sQuery(id+"F0.wireOp",EDGE,"E1.top");var subQ9=sQuery(id+"F0.wireOp",EDGE,"E1.left");var subQ10=sQuery(id+"F0.wireOp",EDGE,"E23.filletArc");var subQ11=sQuery(id+"F0.wireOp",EDGE,"E24.filletArc");Q0=makeQuery(id+"F2.boolean.opBoolean","SPLIT",FACE,{"disambiguationData":[TD([makeQuery(id+"F1.opExtrude","SWEPT_FACE",FACE,{"disambiguationData":[OSD([subQ6])]})])],"derivedFrom":makeQuery(id+"F1.opExtrude","CAP_FACE",FACE,{"disambiguationData":[OSD([subQ6,subQ8,subQ9,subQ7,subQ4,subQ3,subQ2,subQ1,subQ0,subQ5,subQ10,subQ11])],"isStart":true})});}
            var sketch = newSketch(context, id + "F16", { "sketchPlane" : qUnion([Q0])});
            skLineSegment(sketch, "E79", {"start": v(0, 135) * mm, "end": v(0, 165) * mm, "construction": true});
            skCircle(sketch, "E80", {"center": v(0, 165) * mm, "radius": 6 * mm});
            skLineSegment(sketch, "E81", {"start": v(-15, 165) * mm, "end": v(-15, 153) * mm});
            skLineSegment(sketch, "E82", {"start": v(-15, 153) * mm, "end": v(-33, 135) * mm});
            skLineSegment(sketch, "E83", {"start": v(15, 165) * mm, "end": v(15, 153) * mm});
            skLineSegment(sketch, "E84", {"start": v(15, 153) * mm, "end": v(33, 135) * mm});
            skArc(sketch, "E85", {"start": v(15, 165) * mm, "mid": v(0, 180) * mm, "end": v(-15, 165) * mm});
            skLineSegment(sketch, "E86", {"start": v(-80, 0) * mm, "end": v(80, 0) * mm, "construction": true});
            skLineSegment(sketch, "E87.MirrorCS", {"start": v(15, -153) * mm, "end": v(33, -135) * mm});
            skLineSegment(sketch, "E88.MirrorCS", {"start": v(15, -165) * mm, "end": v(15, -153) * mm});
            skLineSegment(sketch, "E89.MirrorCS", {"start": v(-15, -153) * mm, "end": v(-33, -135) * mm});
            skLineSegment(sketch, "E90.MirrorCS", {"start": v(-15, -165) * mm, "end": v(-15, -153) * mm});
            skCircle(sketch, "E91.MirrorC", {"center": v(0, -165) * mm, "radius": 6 * mm});
            skLineSegment(sketch, "E92.MirrorCS", {"start": v(0, -135) * mm, "end": v(0, -165) * mm, "construction": true});
            skArc(sketch, "E93.MirrorCS", {"start": v(15, -165) * mm, "mid": v(0, -180) * mm, "end": v(-15, -165) * mm});
            skSolve(sketch);
        }
        {
            var Q0;
            Q0=makeQuery(id+"F16.imprint","IMPRINT",FACE,{"disambiguationData":[TD([[makeQuery(id+"F16.imprint","IMPRINT",EDGE,{"derivedFrom":sQuery(id+"F16.wireOp",EDGE,"E93.MirrorCS")}),-1.0]])]});
            var Q1;
            Q1=makeQuery(id+"F16.imprint","IMPRINT",FACE,{"disambiguationData":[TD([[makeQuery(id+"F16.imprint","IMPRINT",EDGE,{"derivedFrom":sQuery(id+"F16.wireOp",EDGE,"E80")}),-1.0]])]});
            var Q2;
            Q2=makeQuery(id+"F16.imprint","IMPRINT",FACE,{"disambiguationData":[TD([[makeQuery(id+"F16.imprint","IMPRINT",EDGE,{"derivedFrom":makeQuery(id+"F1.opExtrude","CAP_EDGE",EDGE,{"disambiguationData":[OSD([sQuery(id+"F0.wireOp",EDGE,"E1.left")])],"isStart":true})}),-1.0]])]});
            var Q3;
            Q3=makeQuery(id+"F2.opExtrude","CAP_FACE",FACE,{"disambiguationData":[OSD([sQuery(id+"F0.wireOp",EDGE,"E12"),sQuery(id+"F0.wireOp",EDGE,"E13"),sQuery(id+"F0.wireOp",EDGE,"E14"),sQuery(id+"F0.wireOp",EDGE,"E15"),sQuery(id+"F0.wireOp",EDGE,"E17.filletArc"),sQuery(id+"F0.wireOp",EDGE,"E18.filletArc"),sQuery(id+"F0.wireOp",EDGE,"E19.filletArc"),sQuery(id+"F0.wireOp",EDGE,"E20.filletArc"),sQuery(id+"F0.wireOp",EDGE,"E25.0"),sQuery(id+"F0.wireOp",EDGE,"E25.1"),sQuery(id+"F0.wireOp",EDGE,"E25.2"),sQuery(id+"F0.wireOp",EDGE,"E25.3"),sQuery(id+"F0.wireOp",EDGE,"E25.4"),sQuery(id+"F0.wireOp",EDGE,"E25.5"),sQuery(id+"F0.wireOp",EDGE,"E25.6"),sQuery(id+"F0.wireOp",EDGE,"E25.7")])],"isStart":false});
            extrude(context, id + "F17", {"entities" : qUnion([Q0, Q1, Q2]), "endBound" : BoundingType.UP_TO_SURFACE, "endBoundEntityFace" : qUnion([Q3]), "depth" : 25 * mm});
        }
    });
